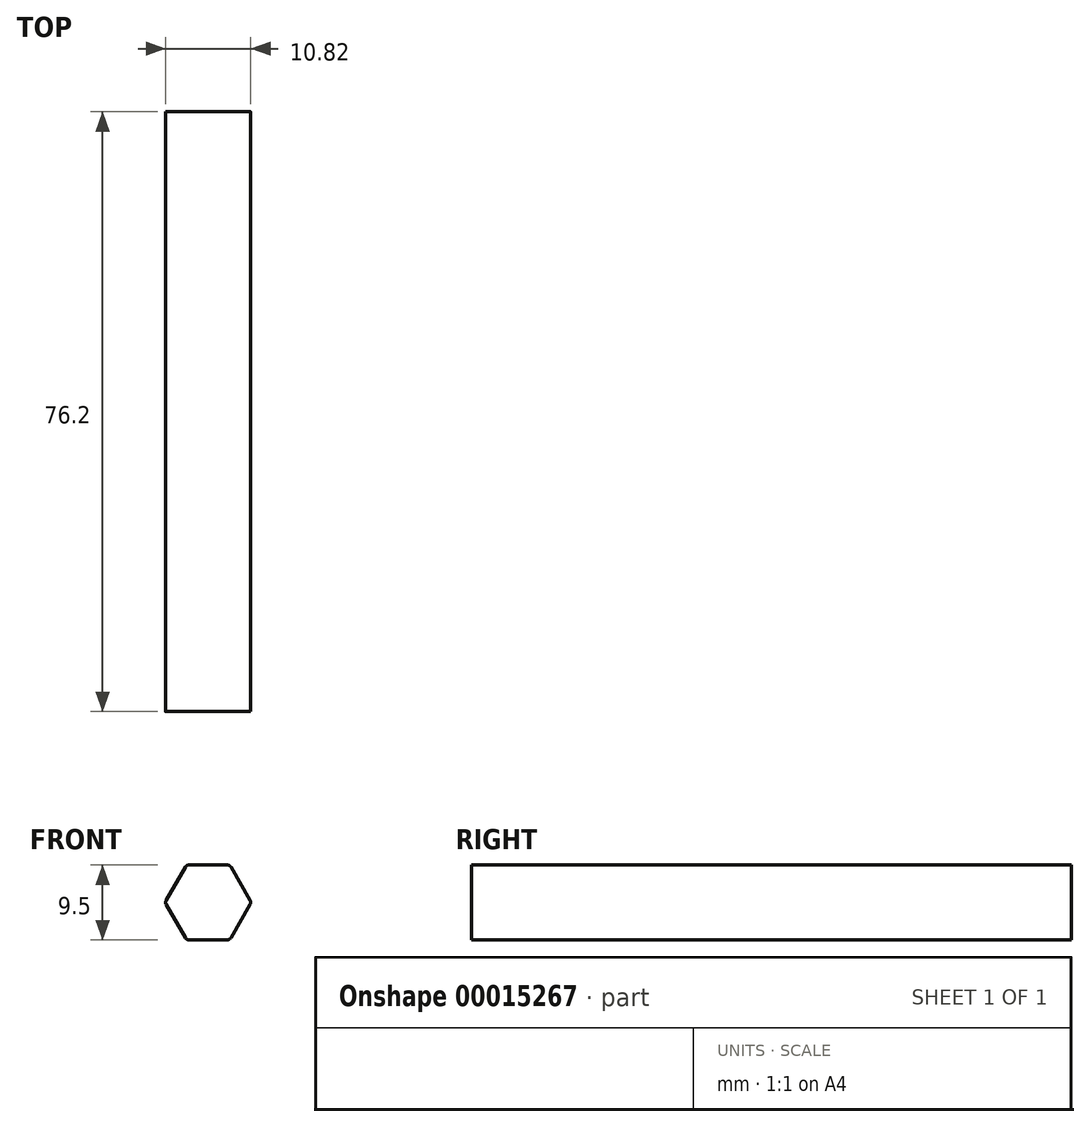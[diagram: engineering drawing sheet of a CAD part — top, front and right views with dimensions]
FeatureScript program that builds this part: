
annotation { "Feature Type Name" : "Feature", "Feature Type Description" : "" }
export const myFeature = defineFeature(function(context is Context, id is Id, definition is map)
    precondition{}
    {
        {
            var Q0;
            Q0=qCreatedBy(makeId("Front.planeOp"),FACE);
            var sketch = newSketch(context, id + "F0", { "sketchPlane" : qUnion([Q0])});
            skCircle(sketch, "E0.cCircle", {"center": v(0, 0) * mm, "radius": 4.75 * mm, "construction": true});
            skLineSegment(sketch, "E0.0", {"start": v(-2.45, 4.75) * mm, "end": v(2.45, 4.75) * mm});
            skLineSegment(sketch, "E0.1", {"start": v(2.89, 4.5) * mm, "end": v(5.34, 0.25) * mm});
            skLineSegment(sketch, "E0.2", {"start": v(5.34, -0.25) * mm, "end": v(2.89, -4.5) * mm});
            skLineSegment(sketch, "E0.3", {"start": v(2.45, -4.75) * mm, "end": v(-2.45, -4.75) * mm});
            skLineSegment(sketch, "E0.4", {"start": v(-2.89, -4.5) * mm, "end": v(-5.34, -0.25) * mm});
            skLineSegment(sketch, "E0.5", {"start": v(-5.34, 0.25) * mm, "end": v(-2.89, 4.5) * mm});
            skPoint(sketch, "E0.0.midPoint", {"position": v(0, 4.75) * mm});
            skPoint(sketch, "E1.visualSharp", {"position": v(-2.74, 4.75) * mm});
            skArc(sketch, "E1.filletArc", {"start": v(-2.45, 4.75) * mm, "mid": v(-2.7, 4.68) * mm, "end": v(-2.89, 4.5) * mm});
            skPoint(sketch, "E2.visualSharp", {"position": v(2.74, 4.75) * mm});
            skArc(sketch, "E2.filletArc", {"start": v(2.89, 4.5) * mm, "mid": v(2.7, 4.68) * mm, "end": v(2.45, 4.75) * mm});
            skPoint(sketch, "E3.visualSharp", {"position": v(5.48, 0) * mm});
            skArc(sketch, "E3.filletArc", {"start": v(5.34, -0.25) * mm, "mid": v(5.4, 0) * mm, "end": v(5.34, 0.25) * mm});
            skPoint(sketch, "E4.visualSharp", {"position": v(2.74, -4.75) * mm});
            skArc(sketch, "E4.filletArc", {"start": v(2.45, -4.75) * mm, "mid": v(2.7, -4.68) * mm, "end": v(2.89, -4.5) * mm});
            skPoint(sketch, "E5.visualSharp", {"position": v(-2.74, -4.75) * mm});
            skArc(sketch, "E5.filletArc", {"start": v(-2.89, -4.5) * mm, "mid": v(-2.7, -4.68) * mm, "end": v(-2.45, -4.75) * mm});
            skPoint(sketch, "E6.visualSharp", {"position": v(-5.48, 0) * mm});
            skArc(sketch, "E6.filletArc", {"start": v(-5.34, 0.25) * mm, "mid": v(-5.4, 0) * mm, "end": v(-5.34, -0.25) * mm});
            skSolve(sketch);
        }
        {
            var Q0;
            Q0=makeQuery(id+"F0.imprint","IMPRINT",FACE,{"disambiguationData":[TD([[makeQuery(id+"F0.imprint","IMPRINT",EDGE,{"derivedFrom":sQuery(id+"F0.wireOp",EDGE,"E0.0")}),-1.0]])]});
            extrude(context, id + "F1", {"entities" : qUnion([Q0]), "depth" : 76.2 * mm});
        }
    });
